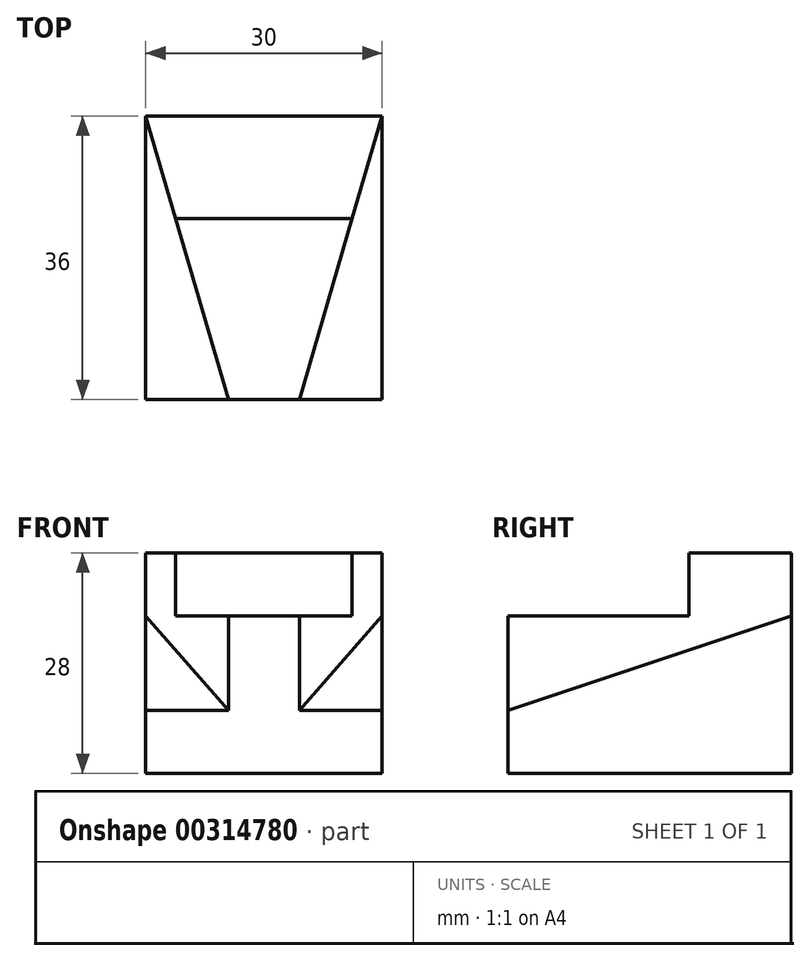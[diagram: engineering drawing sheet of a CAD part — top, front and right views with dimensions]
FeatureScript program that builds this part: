
annotation { "Feature Type Name" : "Feature", "Feature Type Description" : "" }
export const myFeature = defineFeature(function(context is Context, id is Id, definition is map)
    precondition{}
    {
        {
            var Q0;
            Q0=qCreatedBy(makeId("Right.planeOp"),FACE);
            var sketch = newSketch(context, id + "F0", { "sketchPlane" : qUnion([Q0])});
            skLineSegment(sketch, "E0.bottom", {"start": v(0, 0) * mm, "end": v(36, 0) * mm});
            skLineSegment(sketch, "E0.top", {"start": v(0, 30) * mm, "end": v(36, 30) * mm});
            skLineSegment(sketch, "E0.left", {"start": v(0, 0) * mm, "end": v(0, 30) * mm});
            skLineSegment(sketch, "E0.right", {"start": v(36, 0) * mm, "end": v(36, 30) * mm});
            skLineSegment(sketch, "E1.bottom", {"start": v(0, 30) * mm, "end": v(23, 30) * mm});
            skLineSegment(sketch, "E1.top", {"start": v(0, 20) * mm, "end": v(23, 20) * mm});
            skLineSegment(sketch, "E1.left", {"start": v(0, 30) * mm, "end": v(0, 20) * mm});
            skLineSegment(sketch, "E1.right", {"start": v(23, 30) * mm, "end": v(23, 20) * mm});
            skLineSegment(sketch, "E2", {"start": v(36, 20) * mm, "end": v(0, 8) * mm});
            skSolve(sketch);
        }
        {
            var Q0;
            {var subQ0=sQuery(id+"F0.wireOp",EDGE,"E0.bottom");Q0=makeQuery(id+"F0.imprint","IMPRINT",FACE,{"disambiguationData":[TD([[makeQuery(id+"F0.imprint","IMPRINT",EDGE,{"derivedFrom":subQ0}),1.0]])]});}
            extrude(context, id + "F1", {"entities" : qUnion([Q0]), "depth" : 30 * mm, "symmetric" : true});
        }
        {
            var Q0;
            Q0=makeQuery(id+"F1.opExtrude","SWEPT_FACE",FACE,{"disambiguationData":[OSD([sQuery(id+"F0.wireOp",EDGE,"E0.bottom")])]});
            var sketch = newSketch(context, id + "F2", { "sketchPlane" : qUnion([Q0])});
            skLineSegment(sketch, "E3", {"start": v(-4.5, 0) * mm, "end": v(-15, -36) * mm});
            skLineSegment(sketch, "E4", {"start": v(4.5, 0) * mm, "end": v(15, -36) * mm});
            skSolve(sketch);
        }
        {
            var Q0;
            {var subQ0=sQuery(id+"F2.wireOp",EDGE,"E3");Q0=makeQuery(id+"F2.imprint","IMPRINT",FACE,{"disambiguationData":[TD([[makeQuery(id+"F2.imprint","IMPRINT",EDGE,{"derivedFrom":subQ0}),1.0]])]});}
            extrude(context, id + "F3", {"entities" : qUnion([Q0]), "operationType" : NewBodyOperationType.ADD, "flatOperationType" : FlatOperationType.REMOVE, "oppositeDirection" : true, "offsetDistance" : 25 * mm, "depth" : 28 * mm, "domain" : OperationDomain.MODEL});
        }
        {
            var Q0;
            {var subQ4=sQuery(id+"F0.wireOp",EDGE,"E1.top");Q0=makeQuery(id+"F0.imprint","IMPRINT",FACE,{"disambiguationData":[TD([[makeQuery(id+"F0.imprint","IMPRINT",EDGE,{"derivedFrom":subQ4}),1.0]])]});}
            extrude(context, id + "F4", {"entities" : qUnion([Q0]), "operationType" : NewBodyOperationType.REMOVE, "oppositeDirection" : true, "depth" : 30 * mm, "symmetric" : true});
        }
    });
